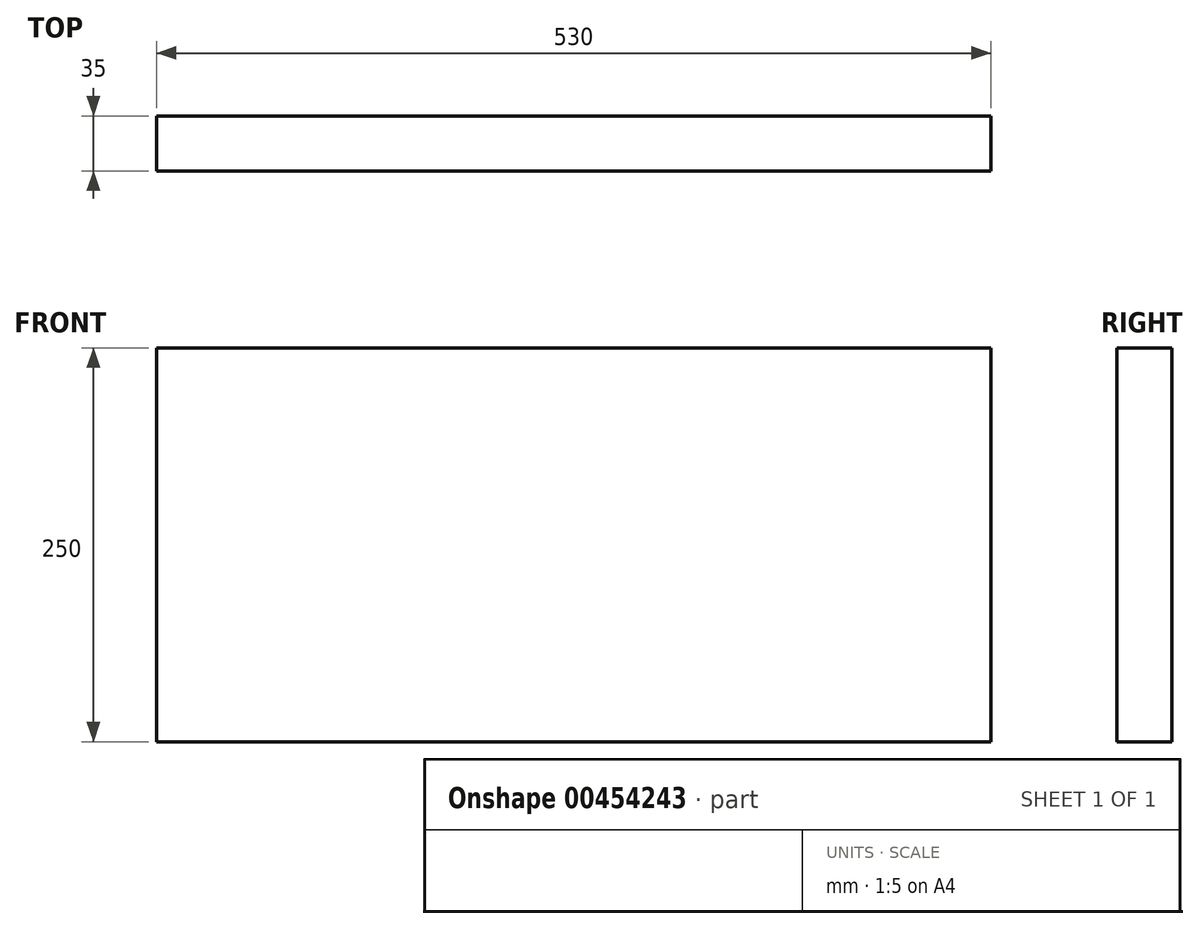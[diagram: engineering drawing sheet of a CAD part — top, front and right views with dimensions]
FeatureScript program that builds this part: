
annotation { "Feature Type Name" : "Feature", "Feature Type Description" : "" }
export const myFeature = defineFeature(function(context is Context, id is Id, definition is map)
    precondition{}
    {
        {
            var Q0;
            Q0=qCreatedBy(makeId("Front.planeOp"),FACE);
            var sketch = newSketch(context, id + "F0", { "sketchPlane" : qUnion([Q0])});
            skLineSegment(sketch, "E0.bottom", {"start": v(-265, 125) * mm, "end": v(265, 125) * mm});
            skLineSegment(sketch, "E0.top", {"start": v(-265, -125) * mm, "end": v(265, -125) * mm});
            skLineSegment(sketch, "E0.left", {"start": v(-265, 125) * mm, "end": v(-265, -125) * mm});
            skLineSegment(sketch, "E0.right", {"start": v(265, 125) * mm, "end": v(265, -125) * mm});
            skPoint(sketch, "E0.middle", {"position": v(0, 0) * mm});
            skSolve(sketch);
        }
        {
            var Q0;
            Q0=makeQuery(id+"F0.imprint","IMPRINT",FACE,{"disambiguationData":[TD([[makeQuery(id+"F0.imprint","IMPRINT",EDGE,{"derivedFrom":sQuery(id+"F0.wireOp",EDGE,"E0.bottom")}),-1.0]])]});
            extrude(context, id + "F1", {"entities" : qUnion([Q0]), "depth" : 35 * mm});
        }
    });
